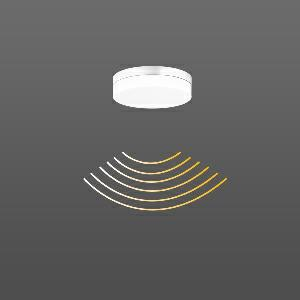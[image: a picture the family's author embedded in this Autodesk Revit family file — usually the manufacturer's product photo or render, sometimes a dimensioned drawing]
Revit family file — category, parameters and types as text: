
# Revit family: flat_slim_round_312135_002_1_19_5a05
name_source: partatom
category: Lighting Fixtures
units: mm (PartAtom-declared; Revit-internal decimal feet)

## family parameters
Cut with Voids When Loaded = No
Host = Face
Light Source = No
Part Type = Normal
Room Calculation Point = No
Round Connector Dimension = Use Diameter
Shared = No

## types (1)
- FLAT SLIM round (1 x LED Modul 840, 1100 lm, 4000)
    Apparent Load = 12 VA
    CIE Flux Codes = 43 74 92 91 100
    Color Rendering = 80
    Color Temperature = 4000
    Default Elevation = 1800 mm
    Height = 63 mm
    Lamp = 1 x LED Modul 840
    Lamp Light Flux = 1100 lm
    Lamp count = 1
    Length = 230 mm
    Lifetime = 50000 h
    Luminous efficacy = 92 lm/W
    Manufacturer = RZB
    ModVariant = No
    Model = 312135.002.1.19
    Mounting Place = Ceiling, Wall
    Mounting Type = Surface mounted
    Number of Poles = 1
    OnlyDefault = Yes
    Power Factor = 1
    Product Name = FLAT SLIM round
    Product group = Surface mounted ceiling and wall luminaires
    ProductGroupID = 305
    Protection Class = Protection class I
    Protection Degree = IP 65
    RLX_Detail_Level = 1
    RLX_Emergency_Light_Flux = 0 lm
    RLX_Emergency_Type = 0
    RLX_Emergency_Type_DB = No
    RlxData = <blob elided: 32049 chars, md5=a55e0d4c>
    Socket = socket
    Standby Power = 0 W
    System Light Flux = 1100 lm
    System Power = 12 W
    Type Comments = Product without accessories
    Type Image = 312132.002.19.jpg
    URL = http://relux.com
    VarID = ---
    Voltage = 230 V
    Voltage Range = 220-240 V
    Weight = 0.00 kg
    Width = 0 mm  [stored 0 ft]

note: [stored X ft] marks values corroborated as IEEE doubles in the binary element streams (Revit-internal decimal feet)

## geometry (parser evidence)
native form markers: Blend x4, Sweep x13
no freeform markers — native parametric forms only
